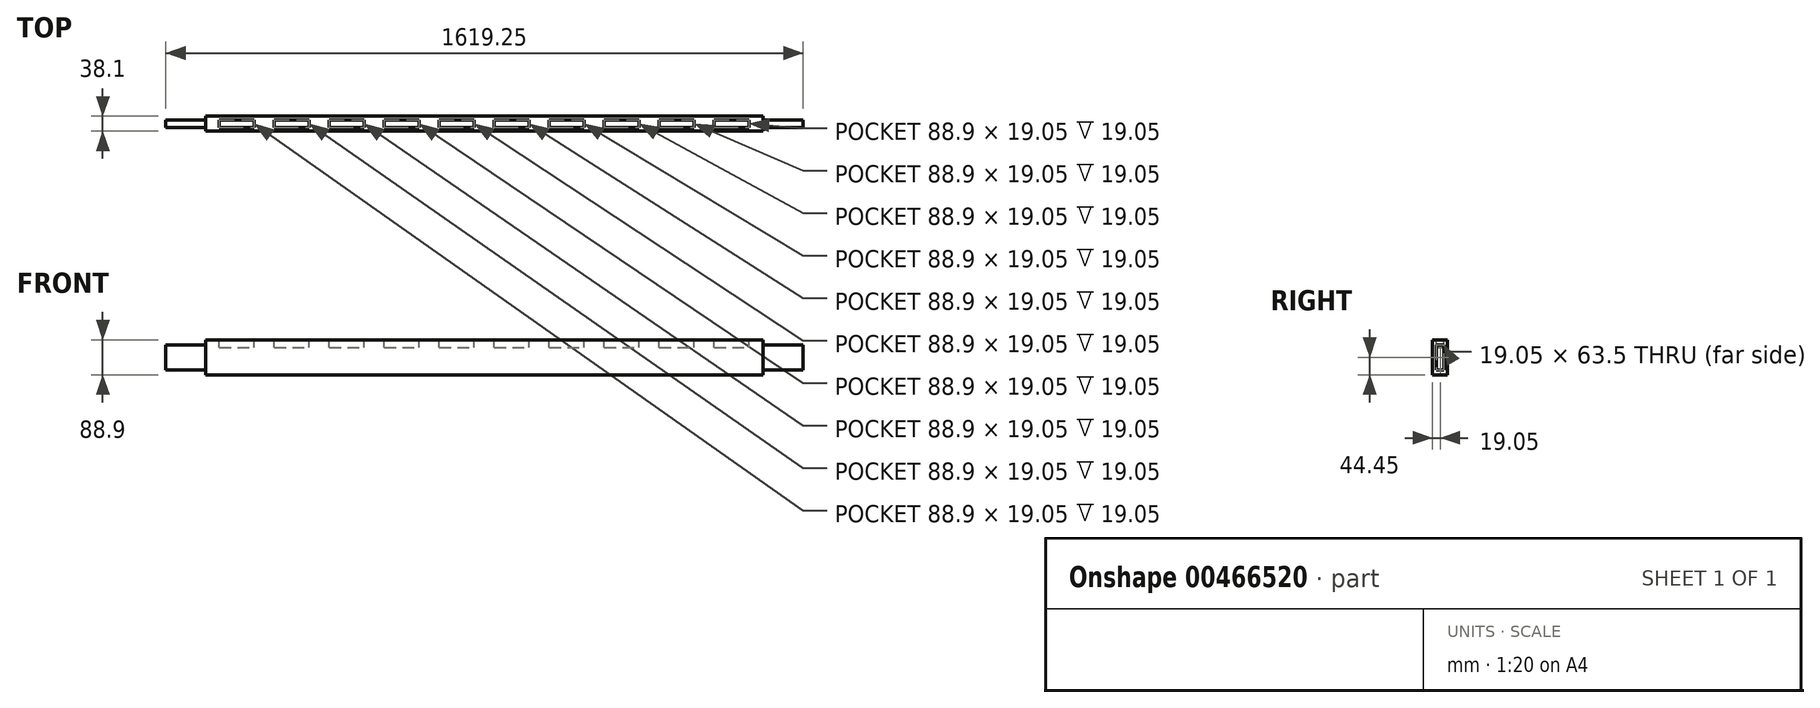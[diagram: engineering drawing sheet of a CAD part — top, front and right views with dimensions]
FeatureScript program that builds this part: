
annotation { "Feature Type Name" : "Feature", "Feature Type Description" : "" }
export const myFeature = defineFeature(function(context is Context, id is Id, definition is map)
    precondition{}
    {
        {
            var Q0;
            Q0=qCreatedBy(makeId("Right.planeOp"),FACE);
            var sketch = newSketch(context, id + "F0", { "sketchPlane" : qUnion([Q0])});
            skLineSegment(sketch, "E0.bottom", {"start": v(19.05, 44.45) * mm, "end": v(-19.05, 44.45) * mm});
            skLineSegment(sketch, "E0.top", {"start": v(19.05, -44.45) * mm, "end": v(-19.05, -44.45) * mm});
            skLineSegment(sketch, "E0.left", {"start": v(19.05, 44.45) * mm, "end": v(19.05, -44.45) * mm});
            skLineSegment(sketch, "E0.right", {"start": v(-19.05, 44.45) * mm, "end": v(-19.05, -44.45) * mm});
            skPoint(sketch, "E0.middle", {"position": v(0, 0) * mm});
            skSolve(sketch);
        }
        {
            var Q0;
            Q0=makeQuery(id+"F0.imprint","IMPRINT",FACE,{"disambiguationData":[TD([[makeQuery(id+"F0.imprint","IMPRINT",EDGE,{"derivedFrom":sQuery(id+"F0.wireOp",EDGE,"E0.bottom")}),1.0]])]});
            extrude(context, id + "F1", {"entities" : qUnion([Q0]), "depth" : 1416.05 * mm});
        }
        {
            var Q0;
            Q0=makeQuery(id+"F1.opExtrude","CAP_FACE",FACE,{"disambiguationData":[OSD([sQuery(id+"F0.wireOp",EDGE,"E0.bottom"),sQuery(id+"F0.wireOp",EDGE,"E0.top"),sQuery(id+"F0.wireOp",EDGE,"E0.left"),sQuery(id+"F0.wireOp",EDGE,"E0.right")])],"isStart":true});
            var sketch = newSketch(context, id + "F2", { "sketchPlane" : qUnion([Q0])});
            skLineSegment(sketch, "E1.bottom", {"start": v(-9.53, 31.75) * mm, "end": v(9.52, 31.75) * mm});
            skLineSegment(sketch, "E1.top", {"start": v(-9.53, -31.75) * mm, "end": v(9.52, -31.75) * mm});
            skLineSegment(sketch, "E1.left", {"start": v(-9.53, 31.75) * mm, "end": v(-9.53, -31.75) * mm});
            skLineSegment(sketch, "E1.right", {"start": v(9.52, 31.75) * mm, "end": v(9.52, -31.75) * mm});
            skPoint(sketch, "E1.middle", {"position": v(0, 0) * mm});
            skSolve(sketch);
        }
        {
            var Q0;
            Q0=makeQuery(id+"F2.imprint","IMPRINT",FACE,{"disambiguationData":[TD([[makeQuery(id+"F2.imprint","IMPRINT",EDGE,{"derivedFrom":sQuery(id+"F2.wireOp",EDGE,"E1.bottom")}),-1.0]])]});
            extrude(context, id + "F3", {"entities" : qUnion([Q0]), "operationType" : NewBodyOperationType.ADD, "depth" : 101.6 * mm});
        }
        {
            var Q0;
            Q0=makeQuery(id+"F1.opExtrude","CAP_FACE",FACE,{"disambiguationData":[OSD([sQuery(id+"F0.wireOp",EDGE,"E0.bottom"),sQuery(id+"F0.wireOp",EDGE,"E0.top"),sQuery(id+"F0.wireOp",EDGE,"E0.left"),sQuery(id+"F0.wireOp",EDGE,"E0.right")])],"isStart":false});
            var sketch = newSketch(context, id + "F4", { "sketchPlane" : qUnion([Q0])});
            skLineSegment(sketch, "E2.bottom", {"start": v(-9.52, 31.75) * mm, "end": v(9.53, 31.75) * mm});
            skLineSegment(sketch, "E2.top", {"start": v(-9.53, -31.75) * mm, "end": v(9.52, -31.75) * mm});
            skLineSegment(sketch, "E2.left", {"start": v(-9.53, 31.75) * mm, "end": v(-9.53, -31.75) * mm});
            skLineSegment(sketch, "E2.right", {"start": v(9.53, 31.75) * mm, "end": v(9.53, -31.75) * mm});
            skPoint(sketch, "E2.middle", {"position": v(0, 0) * mm});
            skSolve(sketch);
        }
        {
            var Q0;
            Q0 = qSketchRegion(id + "F4", true);
            extrude(context, id + "F5", {"entities" : qUnion([Q0]), "operationType" : NewBodyOperationType.ADD, "depth" : 101.6 * mm});
        }
        {
            var Q0;
            Q0=makeQuery(id+"F1.opExtrude","SWEPT_FACE",FACE,{"disambiguationData":[OSD([sQuery(id+"F0.wireOp",EDGE,"E0.bottom")])]});
            var sketch = newSketch(context, id + "F6", { "sketchPlane" : qUnion([Q0])});
            skLineSegment(sketch, "E3.bottom", {"start": v(34.54, -9.52) * mm, "end": v(123.44, -9.52) * mm});
            skLineSegment(sketch, "E3.top", {"start": v(34.54, 9.53) * mm, "end": v(123.44, 9.53) * mm});
            skLineSegment(sketch, "E3.left", {"start": v(34.54, -9.52) * mm, "end": v(34.54, 9.53) * mm});
            skLineSegment(sketch, "E3.right", {"start": v(123.44, -9.52) * mm, "end": v(123.44, 9.53) * mm});
            skPoint(sketch, "E3.middle", {"position": v(79, 0) * mm});
            skLineSegment(sketch, "E4.1.0.0", {"start": v(174.24, -9.52) * mm, "end": v(263.14, -9.52) * mm});
            skLineSegment(sketch, "E4.1.0.1", {"start": v(174.24, -9.52) * mm, "end": v(174.24, 9.53) * mm});
            skLineSegment(sketch, "E4.1.0.2", {"start": v(174.24, 9.53) * mm, "end": v(263.14, 9.53) * mm});
            skLineSegment(sketch, "E4.1.0.3", {"start": v(263.14, -9.52) * mm, "end": v(263.14, 9.53) * mm});
            skLineSegment(sketch, "E4.2.0.0", {"start": v(313.94, -9.52) * mm, "end": v(402.84, -9.52) * mm});
            skLineSegment(sketch, "E4.2.0.1", {"start": v(313.94, -9.52) * mm, "end": v(313.94, 9.53) * mm});
            skLineSegment(sketch, "E4.2.0.2", {"start": v(313.94, 9.53) * mm, "end": v(402.84, 9.53) * mm});
            skLineSegment(sketch, "E4.2.0.3", {"start": v(402.84, -9.52) * mm, "end": v(402.84, 9.53) * mm});
            skLineSegment(sketch, "E4.3.0.0", {"start": v(453.64, -9.52) * mm, "end": v(542.54, -9.52) * mm});
            skLineSegment(sketch, "E4.3.0.1", {"start": v(453.64, -9.52) * mm, "end": v(453.64, 9.53) * mm});
            skLineSegment(sketch, "E4.3.0.2", {"start": v(453.64, 9.53) * mm, "end": v(542.54, 9.53) * mm});
            skLineSegment(sketch, "E4.3.0.3", {"start": v(542.54, -9.52) * mm, "end": v(542.54, 9.53) * mm});
            skLineSegment(sketch, "E4.4.0.0", {"start": v(593.34, -9.52) * mm, "end": v(682.24, -9.52) * mm});
            skLineSegment(sketch, "E4.4.0.1", {"start": v(593.34, -9.52) * mm, "end": v(593.34, 9.53) * mm});
            skLineSegment(sketch, "E4.4.0.2", {"start": v(593.34, 9.53) * mm, "end": v(682.24, 9.53) * mm});
            skLineSegment(sketch, "E4.4.0.3", {"start": v(682.24, -9.52) * mm, "end": v(682.24, 9.53) * mm});
            skLineSegment(sketch, "E4.5.0.0", {"start": v(733.04, -9.52) * mm, "end": v(821.94, -9.52) * mm});
            skLineSegment(sketch, "E4.5.0.1", {"start": v(733.04, -9.52) * mm, "end": v(733.04, 9.53) * mm});
            skLineSegment(sketch, "E4.5.0.2", {"start": v(733.04, 9.53) * mm, "end": v(821.94, 9.53) * mm});
            skLineSegment(sketch, "E4.5.0.3", {"start": v(821.94, -9.52) * mm, "end": v(821.94, 9.53) * mm});
            skLineSegment(sketch, "E4.6.0.0", {"start": v(872.74, -9.52) * mm, "end": v(961.64, -9.52) * mm});
            skLineSegment(sketch, "E4.6.0.1", {"start": v(872.74, -9.52) * mm, "end": v(872.74, 9.53) * mm});
            skLineSegment(sketch, "E4.6.0.2", {"start": v(872.74, 9.53) * mm, "end": v(961.64, 9.53) * mm});
            skLineSegment(sketch, "E4.6.0.3", {"start": v(961.64, -9.52) * mm, "end": v(961.64, 9.53) * mm});
            skLineSegment(sketch, "E4.7.0.0", {"start": v(1012.44, -9.52) * mm, "end": v(1101.34, -9.52) * mm});
            skLineSegment(sketch, "E4.7.0.1", {"start": v(1012.44, -9.52) * mm, "end": v(1012.44, 9.53) * mm});
            skLineSegment(sketch, "E4.7.0.2", {"start": v(1012.44, 9.53) * mm, "end": v(1101.34, 9.53) * mm});
            skLineSegment(sketch, "E4.7.0.3", {"start": v(1101.34, -9.52) * mm, "end": v(1101.34, 9.53) * mm});
            skLineSegment(sketch, "E4.8.0.0", {"start": v(1152.14, -9.52) * mm, "end": v(1241.04, -9.52) * mm});
            skLineSegment(sketch, "E4.8.0.1", {"start": v(1152.14, -9.52) * mm, "end": v(1152.14, 9.53) * mm});
            skLineSegment(sketch, "E4.8.0.2", {"start": v(1152.14, 9.53) * mm, "end": v(1241.04, 9.53) * mm});
            skLineSegment(sketch, "E4.8.0.3", {"start": v(1241.04, -9.52) * mm, "end": v(1241.04, 9.53) * mm});
            skLineSegment(sketch, "E4.9.0.0", {"start": v(1291.84, -9.52) * mm, "end": v(1380.74, -9.52) * mm});
            skLineSegment(sketch, "E4.9.0.1", {"start": v(1291.84, -9.52) * mm, "end": v(1291.84, 9.53) * mm});
            skLineSegment(sketch, "E4.9.0.2", {"start": v(1291.84, 9.53) * mm, "end": v(1380.74, 9.53) * mm});
            skLineSegment(sketch, "E4.9.0.3", {"start": v(1380.74, -9.52) * mm, "end": v(1380.74, 9.53) * mm});
            skLineSegment(sketch, "E4.direction1", {"start": v(34.54, -9.52) * mm, "end": v(174.24, -9.52) * mm, "construction": true});
            skSolve(sketch);
        }
        {
            var Q0;
            Q0 = qSketchRegion(id + "F6", true);
            extrude(context, id + "F7", {"entities" : qUnion([Q0]), "operationType" : NewBodyOperationType.REMOVE, "oppositeDirection" : true, "depth" : 19.05 * mm});
        }
    });
